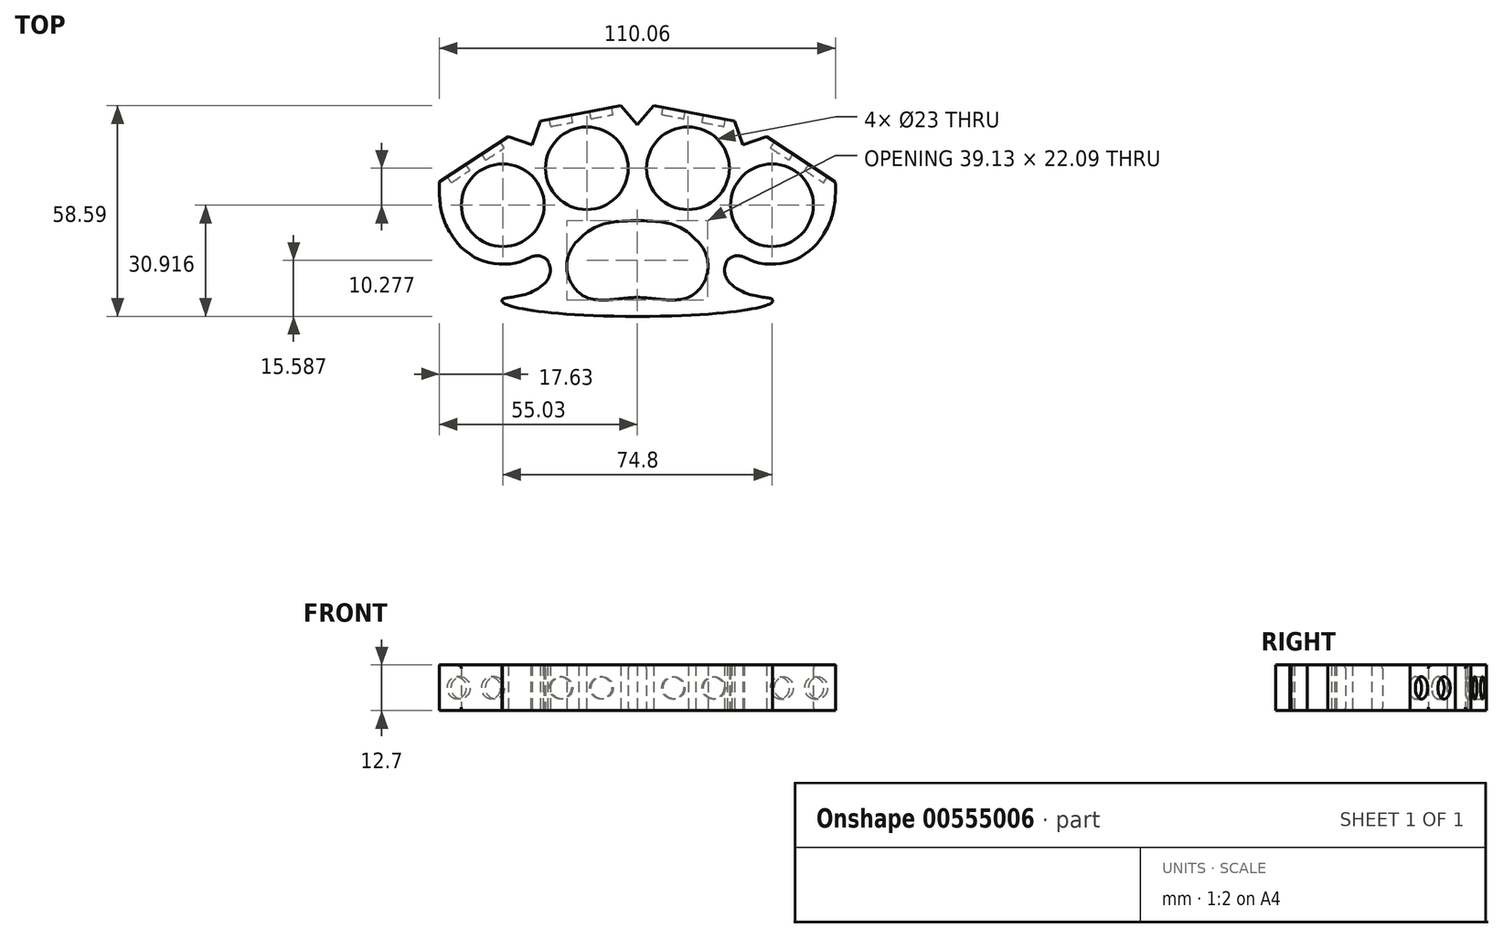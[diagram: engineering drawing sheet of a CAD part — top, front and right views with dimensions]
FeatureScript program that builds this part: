
annotation { "Feature Type Name" : "Feature", "Feature Type Description" : "" }
export const myFeature = defineFeature(function(context is Context, id is Id, definition is map)
    precondition{}
    {
        {
            var Q0;
            Q0=qCreatedBy(makeId("Top.planeOp"),FACE);
            var sketch = newSketch(context, id + "F0", { "sketchPlane" : qUnion([Q0])});
            skCircle(sketch, "E0", {"center": v(-37.4, 3.12) * mm, "radius": 11.5 * mm});
            skCircle(sketch, "E1", {"center": v(-14.05, 13.4) * mm, "radius": 11.5 * mm});
            skArc(sketch, "E2", {"start": v(-26.21, -18.95) * mm, "mid": v(-24.3, -15.84) * mm, "end": v(-25, -12.25) * mm});
            skArc(sketch, "E3.trimOffspring", {"start": v(-50.89, -6.26) * mm, "mid": v(-45.01, -11.44) * mm, "end": v(-37.4, -13.3) * mm});
            skFitSpline(sketch, "E4", {"points": [v(-37.4, -23.36) * mm, v(0, -27.8) * mm], "startDerivative": vector(-5.52, -3.15) * mm, "endDerivative": vector(88.1, 0) * mm});
            skFitSpline(sketch, "E5", {"points": [v(-37.6, -23.56) * mm, v(-26.21, -18.95) * mm], "startDerivative": vector(-0.76, 5.32) * mm, "endDerivative": vector(16.5, 13.97) * mm});
            skArc(sketch, "E6", {"start": v(-37.4, -13.3) * mm, "mid": v(-33.39, -12.81) * mm, "end": v(-29.62, -11.35) * mm});
            skPoint(sketch, "E7.orphan", {"position": v(-33.86, -12.92) * mm});
            skFitSpline(sketch, "E8", {"points": [v(-37.6, -23.56) * mm, v(-37.57, -23.78) * mm], "startDerivative": vector(-0.15, -0.46) * mm, "endDerivative": vector(0.32, -0.68) * mm});
            skArc(sketch, "E9", {"start": v(-25, -12.25) * mm, "mid": v(-27.15, -11) * mm, "end": v(-29.62, -11.35) * mm});
            skFitSpline(sketch, "E10.MirrorCS", {"points": [v(37.6, -23.56) * mm, v(37.57, -23.78) * mm], "startDerivative": vector(0.15, -0.46) * mm, "endDerivative": vector(-0.32, -0.68) * mm});
            skFitSpline(sketch, "E11.MirrorCS", {"points": [v(37.6, -23.56) * mm, v(26.21, -18.95) * mm], "startDerivative": vector(0.76, 5.32) * mm, "endDerivative": vector(-16.5, 13.97) * mm});
            skCircle(sketch, "E12.MirrorC", {"center": v(14.05, 13.4) * mm, "radius": 11.5 * mm});
            skCircle(sketch, "E13.MirrorC", {"center": v(37.4, 3.12) * mm, "radius": 11.5 * mm});
            skArc(sketch, "E14.MirrorCS", {"start": v(25, -12.25) * mm, "mid": v(27.15, -11) * mm, "end": v(29.62, -11.35) * mm});
            skArc(sketch, "E15.MirrorCS", {"start": v(26.21, -18.95) * mm, "mid": v(24.3, -15.84) * mm, "end": v(25, -12.25) * mm});
            skFitSpline(sketch, "E16.MirrorCS", {"points": [v(37.4, -23.36) * mm, v(0, -27.8) * mm], "startDerivative": vector(5.52, -3.15) * mm, "endDerivative": vector(-88.1, 0) * mm});
            skPoint(sketch, "E17.MirrorP", {"position": v(33.86, -12.92) * mm});
            skArc(sketch, "E18.MirrorCS", {"start": v(37.4, -13.3) * mm, "mid": v(33.39, -12.81) * mm, "end": v(29.62, -11.35) * mm});
            skPoint(sketch, "E19.start.orphan", {"position": v(0, 0) * mm});
            skArc(sketch, "E20.MirrorCS", {"start": v(-14.17, -22.56) * mm, "mid": v(-19.55, -15.06) * mm, "end": v(-16.26, -6.44) * mm});
            skFitSpline(sketch, "E21", {"points": [v(-16.26, -6.44) * mm, v(0, -1.17) * mm], "startDerivative": vector(14.63, 14.97) * mm, "endDerivative": vector(21.5, 0.42) * mm});
            skFitSpline(sketch, "E22", {"points": [v(-14.17, -22.56) * mm, v(0, -22.56) * mm], "startDerivative": vector(13.14, -4.8) * mm, "endDerivative": vector(14.17, 0) * mm});
            skFitSpline(sketch, "E23.MirrorCS", {"points": [v(16.26, -6.44) * mm, v(0, -1.17) * mm], "startDerivative": vector(-14.63, 14.97) * mm, "endDerivative": vector(-21.5, 0.42) * mm});
            skFitSpline(sketch, "E24.MirrorCS", {"points": [v(14.17, -22.56) * mm, v(0, -22.56) * mm], "startDerivative": vector(-13.14, -4.8) * mm, "endDerivative": vector(-14.17, 0) * mm});
            skArc(sketch, "E25.MirrorCS", {"start": v(14.17, -22.56) * mm, "mid": v(19.55, -15.06) * mm, "end": v(16.26, -6.44) * mm});
            skArc(sketch, "E26.trimOffspring", {"start": v(50.89, -6.26) * mm, "mid": v(45.01, -11.44) * mm, "end": v(37.4, -13.3) * mm});
            skLineSegment(sketch, "E27", {"start": v(-27, 26.47) * mm, "end": v(-4.58, 30.8) * mm});
            skLineSegment(sketch, "E28", {"start": v(-4.58, 30.8) * mm, "end": v(0, 25.5) * mm});
            skLineSegment(sketch, "E29", {"start": v(-29.29, 19.85) * mm, "end": v(-27, 26.47) * mm});
            skLineSegment(sketch, "E30.MirrorCS", {"start": v(4.58, 30.8) * mm, "end": v(0, 25.5) * mm});
            skLineSegment(sketch, "E31.MirrorCS", {"start": v(27, 26.47) * mm, "end": v(4.58, 30.8) * mm});
            skLineSegment(sketch, "E32.MirrorCS", {"start": v(29.29, 19.85) * mm, "end": v(27, 26.47) * mm});
            skPoint(sketch, "E33.endDerivative.orphan", {"position": v(0, 24.73) * mm});
            skPoint(sketch, "E33.startDerivative.orphan", {"position": v(0, 24.73) * mm});
            skPoint(sketch, "E34.MirrorCS.end.orphan", {"position": v(-29.29, 19.85) * mm});
            skLineSegment(sketch, "E35", {"start": v(-29.29, 19.85) * mm, "end": v(-35.9, 22.14) * mm});
            skLineSegment(sketch, "E36", {"start": v(-35.9, 22.14) * mm, "end": v(-54.99, 9.62) * mm});
            skFitSpline(sketch, "E37", {"points": [v(-54.99, 9.62) * mm, v(-50.89, -6.26) * mm], "startDerivative": vector(-0.66, -19.22) * mm, "endDerivative": vector(11.2, -16.03) * mm});
            skPoint(sketch, "E38.orphan", {"position": v(-53.82, 3.12) * mm});
            skFitSpline(sketch, "E39.MirrorCS", {"points": [v(54.99, 9.62) * mm, v(50.89, -6.26) * mm], "startDerivative": vector(0.66, -19.22) * mm, "endDerivative": vector(-11.2, -16.03) * mm});
            skLineSegment(sketch, "E40.MirrorCS", {"start": v(35.9, 22.14) * mm, "end": v(54.99, 9.62) * mm});
            skLineSegment(sketch, "E41.MirrorCS", {"start": v(29.29, 19.85) * mm, "end": v(35.9, 22.14) * mm});
            skPoint(sketch, "E42.orphan", {"position": v(53.82, 3.12) * mm});
            skSolve(sketch);
        }
        {
            var Q0;
            Q0=makeQuery(id+"F0.imprint","IMPRINT",FACE,{"disambiguationData":[TD([[makeQuery(id+"F0.imprint","IMPRINT",EDGE,{"derivedFrom":sQuery(id+"F0.wireOp",EDGE,"E0")}),-1.0]])]});
            extrude(context, id + "F1", {"entities" : qUnion([Q0]), "endBound" : BoundingType.SYMMETRIC, "depth" : 12.7 * mm, "offsetDistance" : 25 * mm});
        }
        {
            var Q0;
            Q0=makeQuery(id+"F1.opExtrude","SWEPT_FACE",FACE,{"disambiguationData":[OSD([sQuery(id+"F0.wireOp",EDGE,"E40.MirrorCS")])]});
            var sketch = newSketch(context, id + "F2", { "sketchPlane" : qUnion([Q0])});
            skLineSegment(sketch, "E43", {"start": v(-29.29, 6.35) * mm, "end": v(-29.29, -6.35) * mm, "construction": true});
            skLineSegment(sketch, "E44", {"start": v(-29.29, -6.35) * mm, "end": v(-17.87, -6.35) * mm, "construction": true});
            skLineSegment(sketch, "E45", {"start": v(-17.87, -6.35) * mm, "end": v(-29.29, 6.35) * mm, "construction": true});
            skLineSegment(sketch, "E46", {"start": v(-29.29, 6.35) * mm, "end": v(-40.7, -6.35) * mm, "construction": true});
            skLineSegment(sketch, "E47", {"start": v(-40.7, -6.35) * mm, "end": v(-29.29, -6.35) * mm, "construction": true});
            skCircle(sketch, "E48", {"center": v(-35, 0) * mm, "radius": 3.1 * mm});
            skCircle(sketch, "E49", {"center": v(-23.58, 0) * mm, "radius": 3.1 * mm});
            skSolve(sketch);
        }
        {
            var Q0;
            Q0=makeQuery(id+"F2.imprint","IMPRINT",FACE,{"disambiguationData":[TD([[makeQuery(id+"F2.imprint","IMPRINT",EDGE,{"derivedFrom":sQuery(id+"F2.wireOp",EDGE,"E48")}),1.0]])]});
            var Q1;
            Q1=makeQuery(id+"F2.imprint","IMPRINT",FACE,{"disambiguationData":[TD([[makeQuery(id+"F2.imprint","IMPRINT",EDGE,{"derivedFrom":sQuery(id+"F2.wireOp",EDGE,"E49")}),1.0]])]});
            extrude(context, id + "F3", {"entities" : qUnion([Q0, Q1]), "operationType" : NewBodyOperationType.REMOVE, "oppositeDirection" : true, "depth" : 2 * mm, "offsetDistance" : 25 * mm});
        }
        {
            var Q0;
            Q0=makeQuery(id+"F1.opExtrude","SWEPT_FACE",FACE,{"disambiguationData":[OSD([sQuery(id+"F0.wireOp",EDGE,"E31.MirrorCS")])]});
            var sketch = newSketch(context, id + "F4", { "sketchPlane" : qUnion([Q0])});
            skLineSegment(sketch, "E50", {"start": v(1.33, -6.35) * mm, "end": v(-10.08, 6.35) * mm, "construction": true});
            skLineSegment(sketch, "E51", {"start": v(-10.08, 6.35) * mm, "end": v(-21.5, -6.35) * mm, "construction": true});
            skLineSegment(sketch, "E52", {"start": v(-21.5, -6.35) * mm, "end": v(1.33, -6.35) * mm, "construction": true});
            skCircle(sketch, "E53", {"center": v(-15.79, 0) * mm, "radius": 3.1 * mm});
            skCircle(sketch, "E54", {"center": v(-4.38, 0) * mm, "radius": 3.1 * mm});
            skSolve(sketch);
        }
        {
            var Q0;
            Q0=makeQuery(id+"F4.imprint","IMPRINT",FACE,{"disambiguationData":[TD([[makeQuery(id+"F4.imprint","IMPRINT",EDGE,{"derivedFrom":sQuery(id+"F4.wireOp",EDGE,"E53")}),1.0]])]});
            var Q1;
            Q1=makeQuery(id+"F4.imprint","IMPRINT",FACE,{"disambiguationData":[TD([[makeQuery(id+"F4.imprint","IMPRINT",EDGE,{"derivedFrom":sQuery(id+"F4.wireOp",EDGE,"E54")}),1.0]])]});
            extrude(context, id + "F5", {"entities" : qUnion([Q0, Q1]), "operationType" : NewBodyOperationType.REMOVE, "oppositeDirection" : true, "depth" : 2 * mm, "offsetDistance" : 25 * mm});
        }
        {
            var Q0;
            Q0=makeQuery(id+"F1.opExtrude","SWEPT_FACE",FACE,{"disambiguationData":[OSD([sQuery(id+"F0.wireOp",EDGE,"E27")])]});
            var sketch = newSketch(context, id + "F6", { "sketchPlane" : qUnion([Q0])});
            skLineSegment(sketch, "E55", {"start": v(-1.33, -6.35) * mm, "end": v(10.08, 6.35) * mm, "construction": true});
            skLineSegment(sketch, "E56", {"start": v(10.08, 6.35) * mm, "end": v(21.5, -6.35) * mm, "construction": true});
            skLineSegment(sketch, "E57", {"start": v(21.5, -6.35) * mm, "end": v(-1.33, -6.35) * mm, "construction": true});
            skCircle(sketch, "E58", {"center": v(4.38, 0) * mm, "radius": 3.1 * mm});
            skCircle(sketch, "E59", {"center": v(15.79, 0) * mm, "radius": 3.1 * mm});
            skSolve(sketch);
        }
        {
            var Q0;
            Q0=makeQuery(id+"F6.imprint","IMPRINT",FACE,{"disambiguationData":[TD([[makeQuery(id+"F6.imprint","IMPRINT",EDGE,{"derivedFrom":sQuery(id+"F6.wireOp",EDGE,"E58")}),1.0]])]});
            var Q1;
            Q1=makeQuery(id+"F6.imprint","IMPRINT",FACE,{"disambiguationData":[TD([[makeQuery(id+"F6.imprint","IMPRINT",EDGE,{"derivedFrom":sQuery(id+"F6.wireOp",EDGE,"E59")}),1.0]])]});
            extrude(context, id + "F7", {"entities" : qUnion([Q0, Q1]), "operationType" : NewBodyOperationType.REMOVE, "oppositeDirection" : true, "depth" : 2 * mm, "offsetDistance" : 25 * mm});
        }
        {
            var Q0;
            Q0=makeQuery(id+"F1.opExtrude","SWEPT_FACE",FACE,{"disambiguationData":[OSD([sQuery(id+"F0.wireOp",EDGE,"E36")])]});
            var sketch = newSketch(context, id + "F8", { "sketchPlane" : qUnion([Q0])});
            skLineSegment(sketch, "E60", {"start": v(17.87, -6.35) * mm, "end": v(29.29, 6.35) * mm, "construction": true});
            skLineSegment(sketch, "E61", {"start": v(29.29, 6.35) * mm, "end": v(40.7, -6.35) * mm, "construction": true});
            skLineSegment(sketch, "E62", {"start": v(40.7, -6.35) * mm, "end": v(17.87, -6.35) * mm, "construction": true});
            skCircle(sketch, "E63", {"center": v(23.58, 0) * mm, "radius": 3.1 * mm});
            skCircle(sketch, "E64", {"center": v(35, 0) * mm, "radius": 3.1 * mm});
            skSolve(sketch);
        }
        {
            var Q0;
            Q0=makeQuery(id+"F8.imprint","IMPRINT",FACE,{"disambiguationData":[TD([[makeQuery(id+"F8.imprint","IMPRINT",EDGE,{"derivedFrom":sQuery(id+"F8.wireOp",EDGE,"E63")}),1.0]])]});
            var Q1;
            Q1=makeQuery(id+"F8.imprint","IMPRINT",FACE,{"disambiguationData":[TD([[makeQuery(id+"F8.imprint","IMPRINT",EDGE,{"derivedFrom":sQuery(id+"F8.wireOp",EDGE,"E64")}),1.0]])]});
            extrude(context, id + "F9", {"entities" : qUnion([Q0, Q1]), "operationType" : NewBodyOperationType.REMOVE, "oppositeDirection" : true, "depth" : 2 * mm, "offsetDistance" : 25 * mm});
        }
        {
            var Q0;
            Q0=makeQuery(id+"F1.opExtrude","CAP_EDGE",EDGE,{"disambiguationData":[OSD([sQuery(id+"F0.wireOp",EDGE,"E12.MirrorC")])],"isStart":false});
            var Q1;
            Q1=makeQuery(id+"F1.opExtrude","CAP_EDGE",EDGE,{"disambiguationData":[OSD([sQuery(id+"F0.wireOp",EDGE,"E13.MirrorC")])],"isStart":false});
            var Q2;
            Q2=makeQuery(id+"F1.opExtrude","CAP_EDGE",EDGE,{"disambiguationData":[OSD([sQuery(id+"F0.wireOp",EDGE,"E1")])],"isStart":false});
            var Q3;
            Q3=makeQuery(id+"F1.opExtrude","CAP_EDGE",EDGE,{"disambiguationData":[OSD([sQuery(id+"F0.wireOp",EDGE,"E0")])],"isStart":false});
            var Q4;
            Q4=makeQuery(id+"F1.opExtrude","CAP_EDGE",EDGE,{"disambiguationData":[OSD([sQuery(id+"F0.wireOp",EDGE,"E13.MirrorC")])],"isStart":true});
            var Q5;
            Q5=makeQuery(id+"F1.opExtrude","CAP_EDGE",EDGE,{"disambiguationData":[OSD([sQuery(id+"F0.wireOp",EDGE,"E12.MirrorC")])],"isStart":true});
            var Q6;
            Q6=makeQuery(id+"F1.opExtrude","CAP_EDGE",EDGE,{"disambiguationData":[OSD([sQuery(id+"F0.wireOp",EDGE,"E1")])],"isStart":true});
            var Q7;
            Q7=makeQuery(id+"F1.opExtrude","CAP_EDGE",EDGE,{"disambiguationData":[OSD([sQuery(id+"F0.wireOp",EDGE,"E0")])],"isStart":true});
            fillet(context, id + "F10", {"entities" : qUnion([Q0, Q1, Q2, Q3, Q4, Q5, Q6, Q7]), "radius" : 1 * mm, "tangentPropagation" : true, "allowEdgeOverflow" : false});
        }
    });
